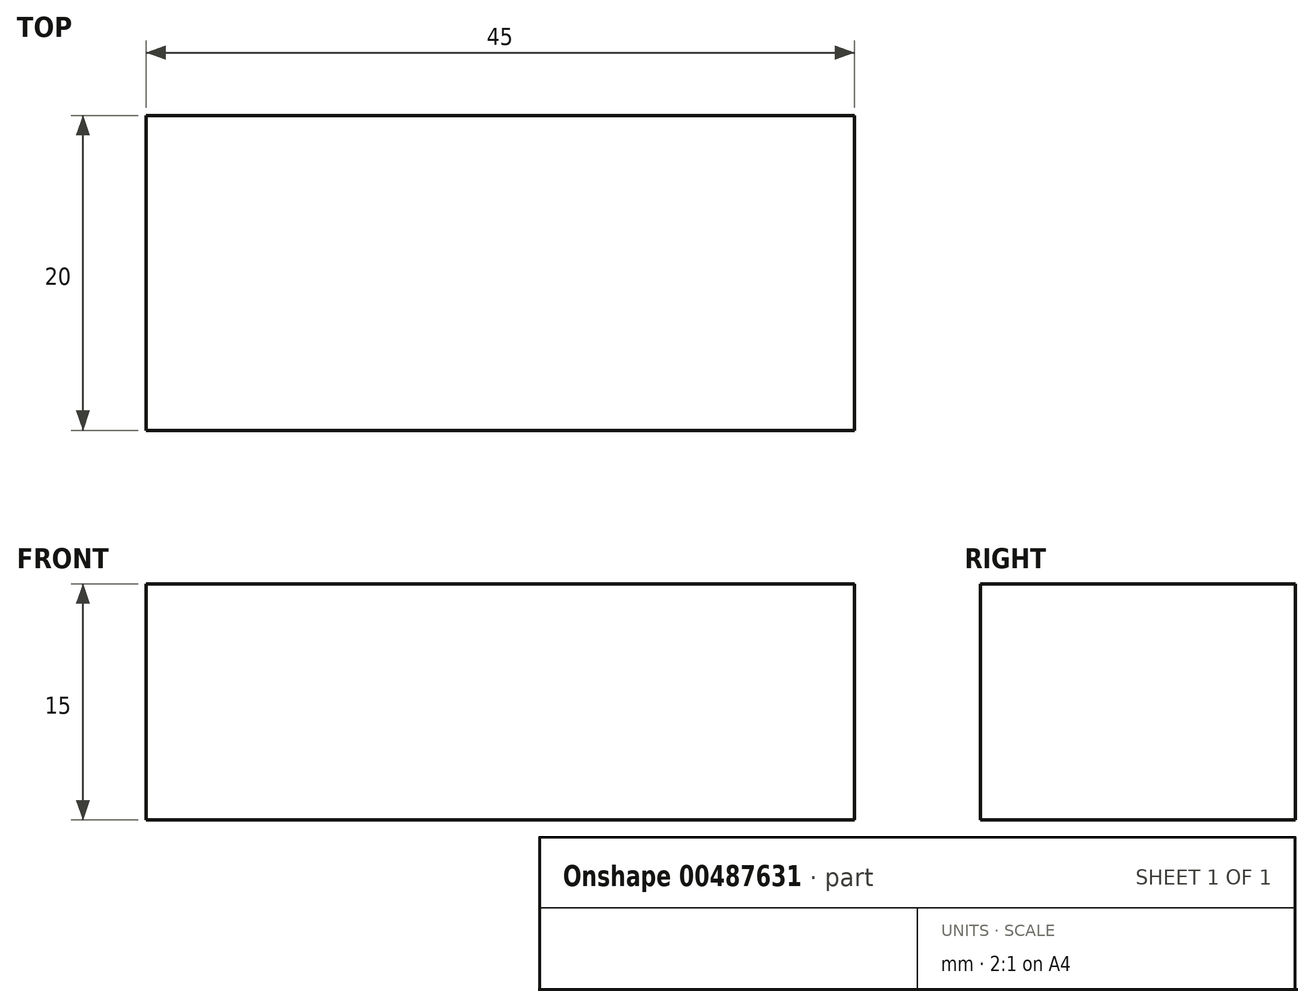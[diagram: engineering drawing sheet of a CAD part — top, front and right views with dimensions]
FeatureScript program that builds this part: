
annotation { "Feature Type Name" : "Feature", "Feature Type Description" : "" }
export const myFeature = defineFeature(function(context is Context, id is Id, definition is map)
    precondition{}
    {
        {
            var Q0;
            Q0=qCreatedBy(makeId("Top.planeOp"),FACE);
            var sketch = newSketch(context, id + "F0", { "sketchPlane" : qUnion([Q0])});
            skLineSegment(sketch, "E0.bottom", {"start": v(22.5, -10) * mm, "end": v(-22.5, -10) * mm});
            skLineSegment(sketch, "E0.top", {"start": v(22.5, 10) * mm, "end": v(-22.5, 10) * mm});
            skLineSegment(sketch, "E0.left", {"start": v(22.5, -10) * mm, "end": v(22.5, 10) * mm});
            skLineSegment(sketch, "E0.right", {"start": v(-22.5, -10) * mm, "end": v(-22.5, 10) * mm});
            skPoint(sketch, "E0.middle", {"position": v(0, 0) * mm});
            skSolve(sketch);
        }
        {
            var Q0;
            Q0 = qSketchRegion(id + "F0", true);
            extrude(context, id + "F1", {"entities" : qUnion([Q0]), "depth" : 15 * mm});
        }
    });
